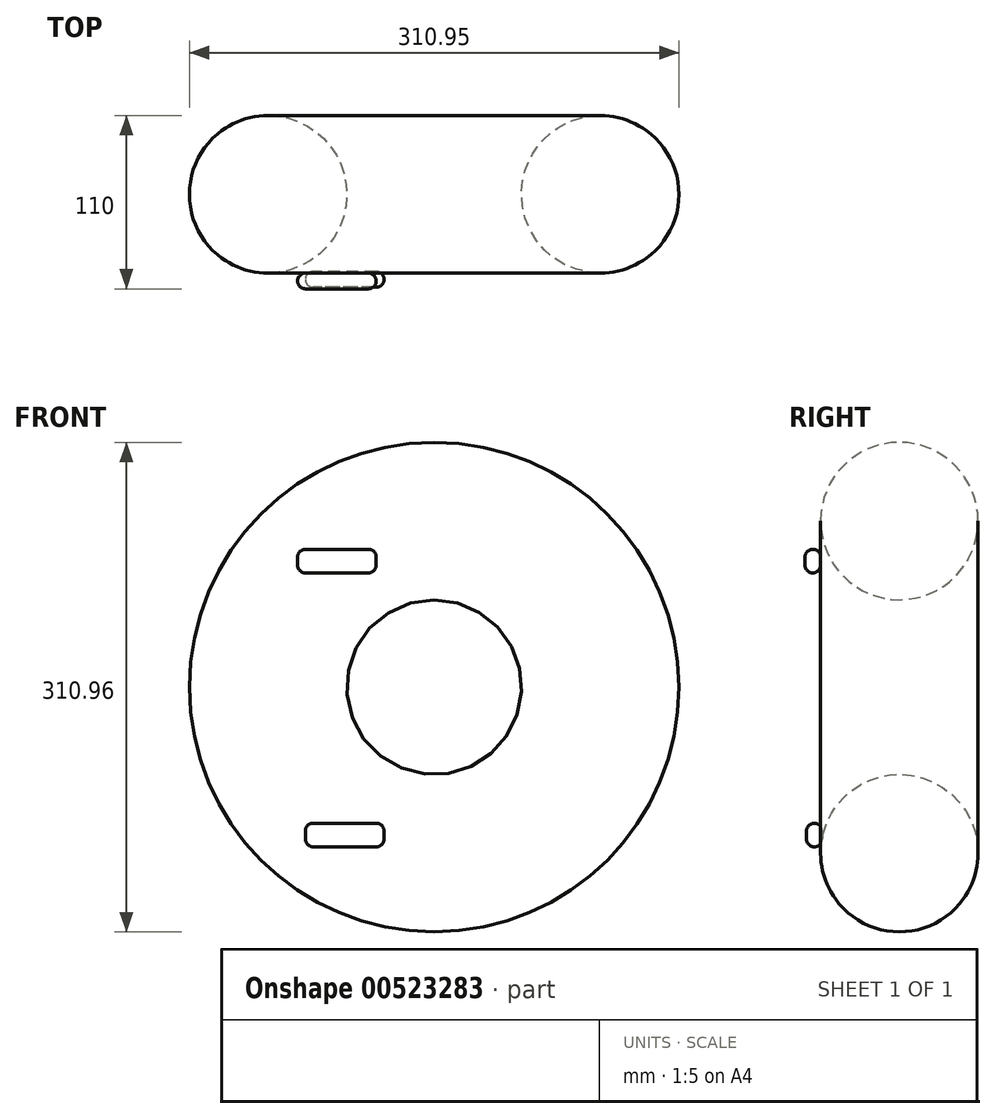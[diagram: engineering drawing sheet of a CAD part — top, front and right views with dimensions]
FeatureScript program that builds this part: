
annotation { "Feature Type Name" : "Feature", "Feature Type Description" : "" }
export const myFeature = defineFeature(function(context is Context, id is Id, definition is map)
    precondition{}
    {
        {
            var Q0;
            Q0=qCreatedBy(makeId("Top.planeOp"),FACE);
            var sketch = newSketch(context, id + "F0", { "sketchPlane" : qUnion([Q0])});
            skCircle(sketch, "E0", {"center": v(0, 0) * mm, "radius": 50 * mm});
            skLineSegment(sketch, "E1", {"start": v(-105.48, 47.74) * mm, "end": v(-105.48, -46) * mm, "construction": true});
            skSolve(sketch);
        }
        {
            var Q0;
            Q0 = qSketchRegion(id + "F0", true);
            var Q1;
            Q1=sQuery(id+"F0.wireOp",EDGE,"E1");
            revolve(context, id + "F1", {"entities" : qUnion([Q0]), "axis" : qUnion([Q1]), "revolveType" : RevolveType.FULL});
        }
        {
            var Q0;
            Q0=qCreatedBy(makeId("Front.planeOp"),FACE);
            cPlane(context, id + "F2", {"entities" : qUnion([Q0]), "cplaneType" : CPlaneType.OFFSET, "offset" : 50 * mm, "width" : 152.4 * mm, "height" : 152.4 * mm});
        }
        {
            var Q0;
            Q0=qCreatedBy(id+"F2.planeOp",FACE);
            var sketch = newSketch(context, id + "F3", { "sketchPlane" : qUnion([Q0])});
            skLineSegment(sketch, "E2.bottom", {"start": v(-142.26, 87.5) * mm, "end": v(-192.26, 87.5) * mm});
            skLineSegment(sketch, "E2.top", {"start": v(-142.26, 72.5) * mm, "end": v(-192.26, 72.5) * mm});
            skLineSegment(sketch, "E2.left", {"start": v(-142.26, 87.5) * mm, "end": v(-142.26, 72.5) * mm});
            skLineSegment(sketch, "E2.right", {"start": v(-192.26, 87.5) * mm, "end": v(-192.26, 72.5) * mm});
            skPoint(sketch, "E2.middle", {"position": v(-167.26, 80) * mm});
            skSolve(sketch);
        }
        {
            var Q0;
            Q0 = qSketchRegion(id + "F3", true);
            extrude(context, id + "F4", {"entities" : qUnion([Q0]), "operationType" : NewBodyOperationType.ADD, "depth" : 10 * mm, "offsetDistance" : 25 * mm});
        }
        {
            var Q0;
            Q0=makeQuery(id+"F4.opExtrude","CAP_EDGE",EDGE,{"disambiguationData":[OSD([sQuery(id+"F3.wireOp",EDGE,"E2.right")])],"isStart":false});
            var Q1;
            Q1=makeQuery(id+"F4.opExtrude","SWEPT_FACE",FACE,{"disambiguationData":[OSD([sQuery(id+"F3.wireOp",EDGE,"E2.bottom")])]});
            var Q2;
            Q2=makeQuery(id+"F4.opExtrude","CAP_FACE",FACE,{"disambiguationData":[OSD([sQuery(id+"F3.wireOp",EDGE,"E2.bottom"),sQuery(id+"F3.wireOp",EDGE,"E2.top"),sQuery(id+"F3.wireOp",EDGE,"E2.left"),sQuery(id+"F3.wireOp",EDGE,"E2.right")])],"isStart":false});
            var Q3;
            Q3=makeQuery(id+"F4.opExtrude","SWEPT_FACE",FACE,{"disambiguationData":[OSD([sQuery(id+"F3.wireOp",EDGE,"E2.right")])]});
            var Q4;
            Q4=makeQuery(id+"F4.opExtrude","SWEPT_FACE",FACE,{"disambiguationData":[OSD([sQuery(id+"F3.wireOp",EDGE,"E2.top")])]});
            var Q5;
            Q5=makeQuery(id+"F4.opExtrude","SWEPT_FACE",FACE,{"disambiguationData":[OSD([sQuery(id+"F3.wireOp",EDGE,"E2.left")])]});
            fillet(context, id + "F5", {"entities" : qUnion([Q0, Q1, Q2, Q3, Q4, Q5]), "radius" : 5 * mm, "tangentPropagation" : true, "allowEdgeOverflow" : false});
        }
        {
            var Q0;
            Q0=makeQuery(id+"F4.opExtrude","SWEPT_BODY",BODY,{"disambiguationData":[OSD([sQuery(id+"F3.wireOp",EDGE,"E2.bottom"),sQuery(id+"F3.wireOp",EDGE,"E2.top"),sQuery(id+"F3.wireOp",EDGE,"E2.left"),sQuery(id+"F3.wireOp",EDGE,"E2.right")])]});
            transform(context, id + "F6", {"entities" : qUnion([Q0]), "transformType" : TransformType.TRANSLATION_3D, "dx" : 5 * mm, "dy" : 1 * mm, "dz" : -174 * mm, "makeCopy" : true});
        }
    });
